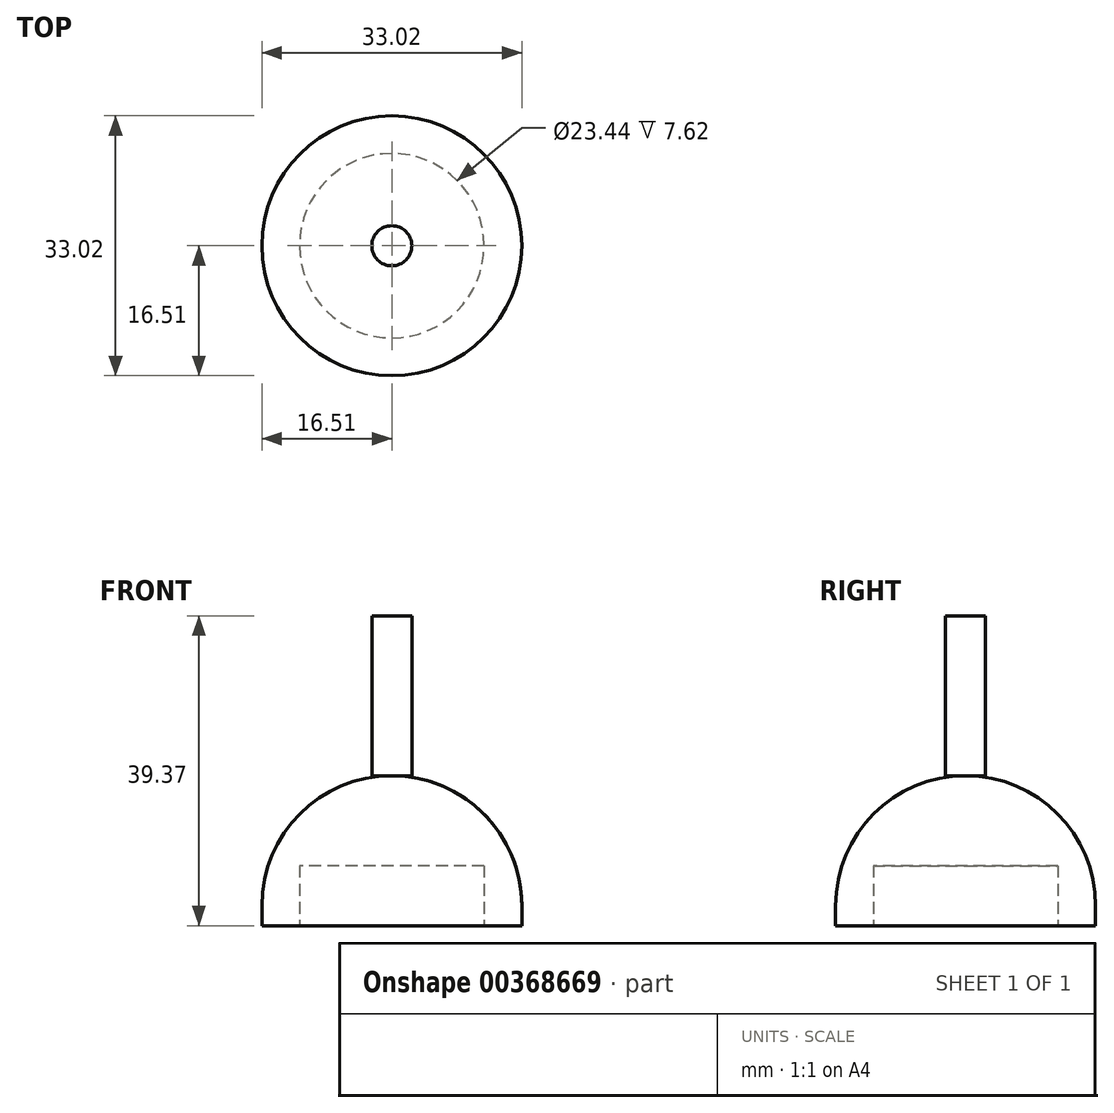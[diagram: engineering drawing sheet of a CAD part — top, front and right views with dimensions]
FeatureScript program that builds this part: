
annotation { "Feature Type Name" : "Feature", "Feature Type Description" : "" }
export const myFeature = defineFeature(function(context is Context, id is Id, definition is map)
    precondition{}
    {
        {
            var Q0;
            Q0=qCreatedBy(makeId("Top.planeOp"),FACE);
            var sketch = newSketch(context, id + "F0", { "sketchPlane" : qUnion([Q0])});
            skCircle(sketch, "E0", {"center": v(0, 0) * mm, "radius": 16.51 * mm});
            skSolve(sketch);
        }
        {
            var Q0;
            Q0 = qSketchRegion(id + "F0", true);
            extrude(context, id + "F1", {"entities" : qUnion([Q0]), "depth" : 19.05 * mm});
        }
        {
            var Q0;
            Q0=makeQuery(id+"F1.opExtrude","CAP_EDGE",EDGE,{"disambiguationData":[OSD([sQuery(id+"F0.wireOp",EDGE,"E0")])],"isStart":false});
            fillet(context, id + "F2", {"entities" : qUnion([Q0]), "radius" : 16.5 * mm, "tangentPropagation" : true, "allowEdgeOverflow" : false});
        }
        {
            var Q0;
            Q0=qCreatedBy(makeId("Top.planeOp"),FACE);
            var sketch = newSketch(context, id + "F3", { "sketchPlane" : qUnion([Q0])});
            skCircle(sketch, "E1", {"center": v(0, 0) * mm, "radius": 11.72 * mm});
            skSolve(sketch);
        }
        {
            var Q0;
            Q0 = qSketchRegion(id + "F3", true);
            extrude(context, id + "F4", {"entities" : qUnion([Q0]), "operationType" : NewBodyOperationType.REMOVE, "depth" : 7.62 * mm});
        }
        {
            var Q0;
            Q0=qCreatedBy(makeId("Top.planeOp"),FACE);
            cPlane(context, id + "F5", {"entities" : qUnion([Q0]), "cplaneType" : CPlaneType.OFFSET, "offset" : 19.05 * mm, "width" : 152.4 * mm, "height" : 152.4 * mm});
        }
        {
            var Q0;
            Q0=qCreatedBy(id+"F5.planeOp",FACE);
            var sketch = newSketch(context, id + "F6", { "sketchPlane" : qUnion([Q0])});
            skCircle(sketch, "E2", {"center": v(0, 0) * mm, "radius": 2.54 * mm});
            skSolve(sketch);
        }
        {
            var Q0;
            Q0 = qSketchRegion(id + "F6", true);
            extrude(context, id + "F7", {"entities" : qUnion([Q0]), "operationType" : NewBodyOperationType.ADD, "depth" : 20.32 * mm});
        }
    });
